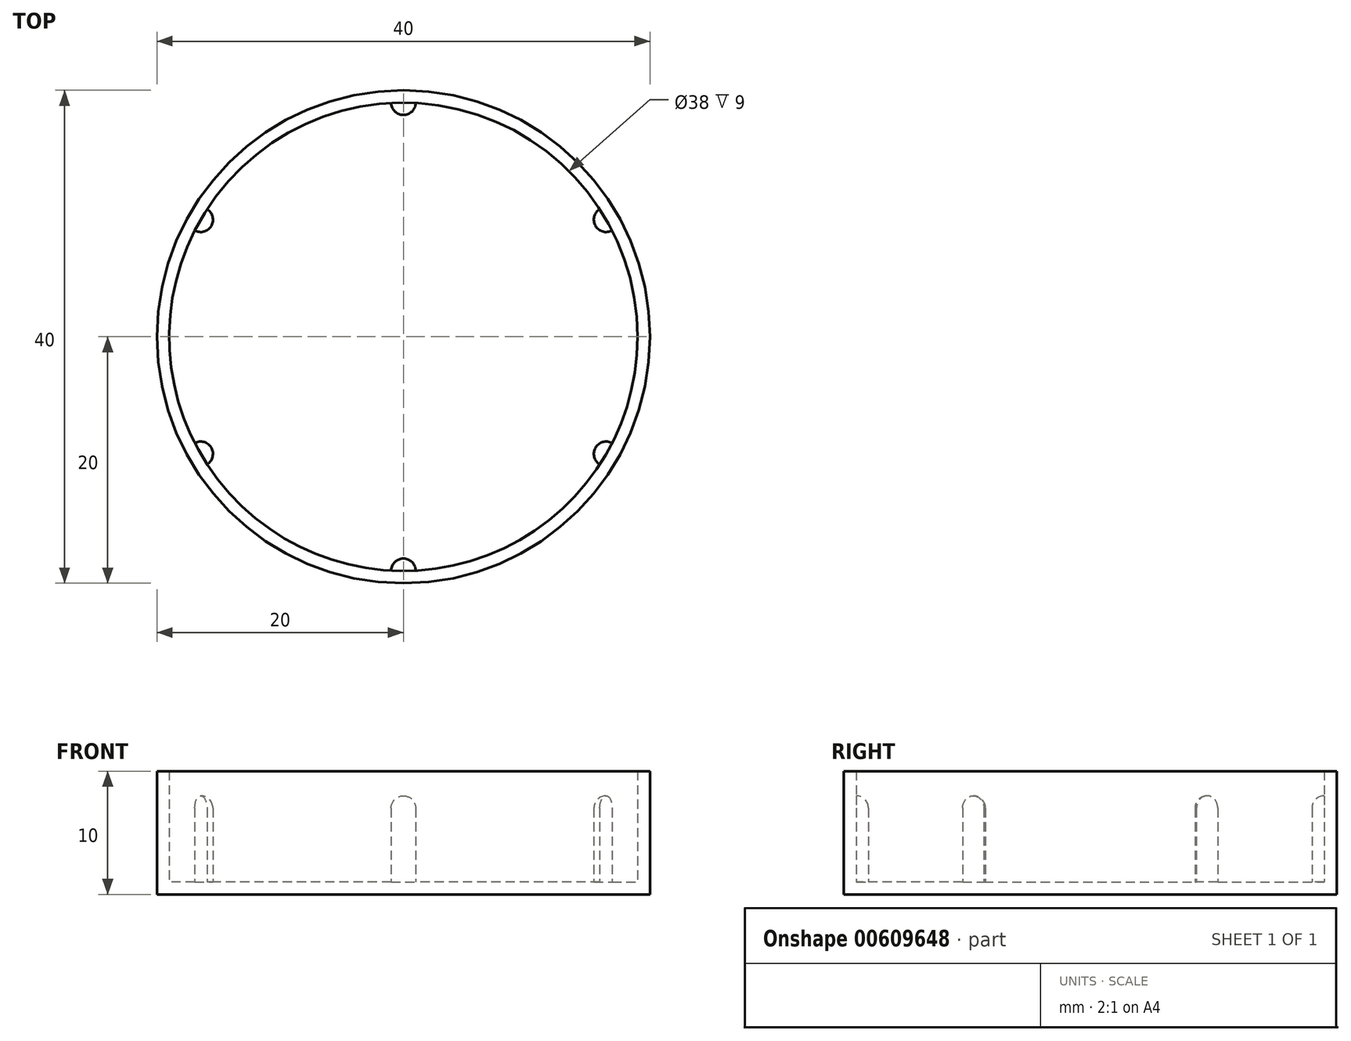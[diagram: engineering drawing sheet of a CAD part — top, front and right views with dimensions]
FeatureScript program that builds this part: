
annotation { "Feature Type Name" : "Feature", "Feature Type Description" : "" }
export const myFeature = defineFeature(function(context is Context, id is Id, definition is map)
    precondition{}
    {
        {
            var Q0;
            Q0=qCreatedBy(makeId("Top.planeOp"),FACE);
            var sketch = newSketch(context, id + "F0", { "sketchPlane" : qUnion([Q0])});
            skCircle(sketch, "E0", {"center": v(0, 0) * mm, "radius": 19 * mm});
            skCircle(sketch, "E1", {"center": v(0, 0) * mm, "radius": 20 * mm});
            skLineSegment(sketch, "E2", {"start": v(0, 0) * mm, "end": v(0, 19) * mm, "construction": true});
            skArc(sketch, "E3", {"start": v(-1, 18.97) * mm, "mid": v(0, 18) * mm, "end": v(1, 18.97) * mm});
            skArc(sketch, "E4.1.0", {"start": v(15.93, 10.35) * mm, "mid": v(15.59, 9) * mm, "end": v(16.93, 8.62) * mm});
            skArc(sketch, "E4.2.0", {"start": v(16.93, -8.62) * mm, "mid": v(15.59, -9) * mm, "end": v(15.93, -10.35) * mm});
            skArc(sketch, "E4.3.0", {"start": v(1, -18.97) * mm, "mid": v(0, -18) * mm, "end": v(-1, -18.97) * mm});
            skArc(sketch, "E4.4.0", {"start": v(-15.93, -10.35) * mm, "mid": v(-15.59, -9) * mm, "end": v(-16.93, -8.62) * mm});
            skArc(sketch, "E4.5.0", {"start": v(-16.93, 8.62) * mm, "mid": v(-15.59, 9) * mm, "end": v(-15.93, 10.35) * mm});
            skLineSegment(sketch, "E4.anchor1", {"start": v(0, 0) * mm, "end": v(-1, 18.97) * mm, "construction": true});
            skLineSegment(sketch, "E4.anchor2", {"start": v(0, 0) * mm, "end": v(-16.93, 8.62) * mm, "construction": true});
            skSolve(sketch);
        }
        {
            var Q0;
            Q0=makeQuery(id+"F0.imprint","IMPRINT",FACE,{"disambiguationData":[TD([[makeQuery(id+"F0.imprint","IMPRINT",EDGE,{"derivedFrom":sQuery(id+"F0.wireOp",EDGE,"E0")}),-1.0]])]});
            var Q1;
            Q1=sQuery(id+"F0.wireOp",EDGE,"E1");
            var Q2;
            Q2=sQuery(id+"F0.wireOp",EDGE,"E0");
            extrude(context, id + "F1", {"entities" : qUnion([Q0]), "surfaceEntities" : qUnion([Q1, Q2]), "depth" : 9 * mm, "offsetDistance" : 25 * mm});
        }
        {
            var Q0;
            Q0=makeQuery(id+"F0.imprint","IMPRINT",FACE,{"disambiguationData":[TD([[makeQuery(id+"F0.imprint","IMPRINT",EDGE,{"derivedFrom":sQuery(id+"F0.wireOp",EDGE,"E0")}),1.0]])]});
            var Q1;
            Q1=makeQuery(id+"F0.imprint","IMPRINT",FACE,{"disambiguationData":[TD([[makeQuery(id+"F0.imprint","IMPRINT",EDGE,{"derivedFrom":sQuery(id+"F0.wireOp",EDGE,"E0")}),-1.0]])]});
            extrude(context, id + "F2", {"entities" : qUnion([Q0, Q1]), "operationType" : NewBodyOperationType.ADD, "oppositeDirection" : true, "depth" : 1 * mm, "offsetDistance" : 25 * mm});
        }
        {
            var Q0;
            {var subQ0=sQuery(id+"F0.wireOp",EDGE,"E4.5.0");Q0=makeQuery(id+"F0.imprint","IMPRINT",FACE,{"disambiguationData":[TD([[makeQuery(id+"F0.imprint","IMPRINT",EDGE,{"derivedFrom":subQ0}),1.0]])]});}
            var Q1;
            {var subQ0=sQuery(id+"F0.wireOp",EDGE,"E3");Q1=makeQuery(id+"F0.imprint","IMPRINT",FACE,{"disambiguationData":[TD([[makeQuery(id+"F0.imprint","IMPRINT",EDGE,{"derivedFrom":subQ0}),1.0]])]});}
            var Q2;
            {var subQ0=sQuery(id+"F0.wireOp",EDGE,"E4.1.0");Q2=makeQuery(id+"F0.imprint","IMPRINT",FACE,{"disambiguationData":[TD([[makeQuery(id+"F0.imprint","IMPRINT",EDGE,{"derivedFrom":subQ0}),1.0]])]});}
            var Q3;
            {var subQ0=sQuery(id+"F0.wireOp",EDGE,"E4.2.0");Q3=makeQuery(id+"F0.imprint","IMPRINT",FACE,{"disambiguationData":[TD([[makeQuery(id+"F0.imprint","IMPRINT",EDGE,{"derivedFrom":subQ0}),1.0]])]});}
            var Q4;
            {var subQ0=sQuery(id+"F0.wireOp",EDGE,"E4.3.0");Q4=makeQuery(id+"F0.imprint","IMPRINT",FACE,{"disambiguationData":[TD([[makeQuery(id+"F0.imprint","IMPRINT",EDGE,{"derivedFrom":subQ0}),1.0]])]});}
            var Q5;
            {var subQ0=sQuery(id+"F0.wireOp",EDGE,"E4.4.0");Q5=makeQuery(id+"F0.imprint","IMPRINT",FACE,{"disambiguationData":[TD([[makeQuery(id+"F0.imprint","IMPRINT",EDGE,{"derivedFrom":subQ0}),1.0]])]});}
            extrude(context, id + "F3", {"entities" : qUnion([Q0, Q1, Q2, Q3, Q4, Q5]), "operationType" : NewBodyOperationType.ADD, "depth" : 7 * mm, "offsetDistance" : 25 * mm, "hasSecondDirection" : true, "secondDirectionOppositeDirection" : true, "secondDirectionDepth" : 1 * mm});
        }
        {
            var Q0;
            Q0=makeQuery(id+"F3.opExtrude","CAP_EDGE",EDGE,{"disambiguationData":[OSD([sQuery(id+"F0.wireOp",EDGE,"E4.1.0")])],"isStart":false});
            var Q1;
            Q1=makeQuery(id+"F3.opExtrude","CAP_EDGE",EDGE,{"disambiguationData":[OSD([sQuery(id+"F0.wireOp",EDGE,"E4.2.0")])],"isStart":false});
            var Q2;
            Q2=makeQuery(id+"F3.opExtrude","CAP_EDGE",EDGE,{"disambiguationData":[OSD([sQuery(id+"F0.wireOp",EDGE,"E4.3.0")])],"isStart":false});
            var Q3;
            Q3=makeQuery(id+"F3.opExtrude","CAP_EDGE",EDGE,{"disambiguationData":[OSD([sQuery(id+"F0.wireOp",EDGE,"E4.4.0")])],"isStart":false});
            var Q4;
            Q4=makeQuery(id+"F3.opExtrude","CAP_EDGE",EDGE,{"disambiguationData":[OSD([sQuery(id+"F0.wireOp",EDGE,"E4.5.0")])],"isStart":false});
            var Q5;
            Q5=makeQuery(id+"F3.opExtrude","CAP_EDGE",EDGE,{"disambiguationData":[OSD([sQuery(id+"F0.wireOp",EDGE,"E3")])],"isStart":false});
            fillet(context, id + "F4", {"entities" : qUnion([Q0, Q1, Q2, Q3, Q4, Q5]), "radius" : 1 * mm, "tangentPropagation" : true, "allowEdgeOverflow" : false});
        }
    });
